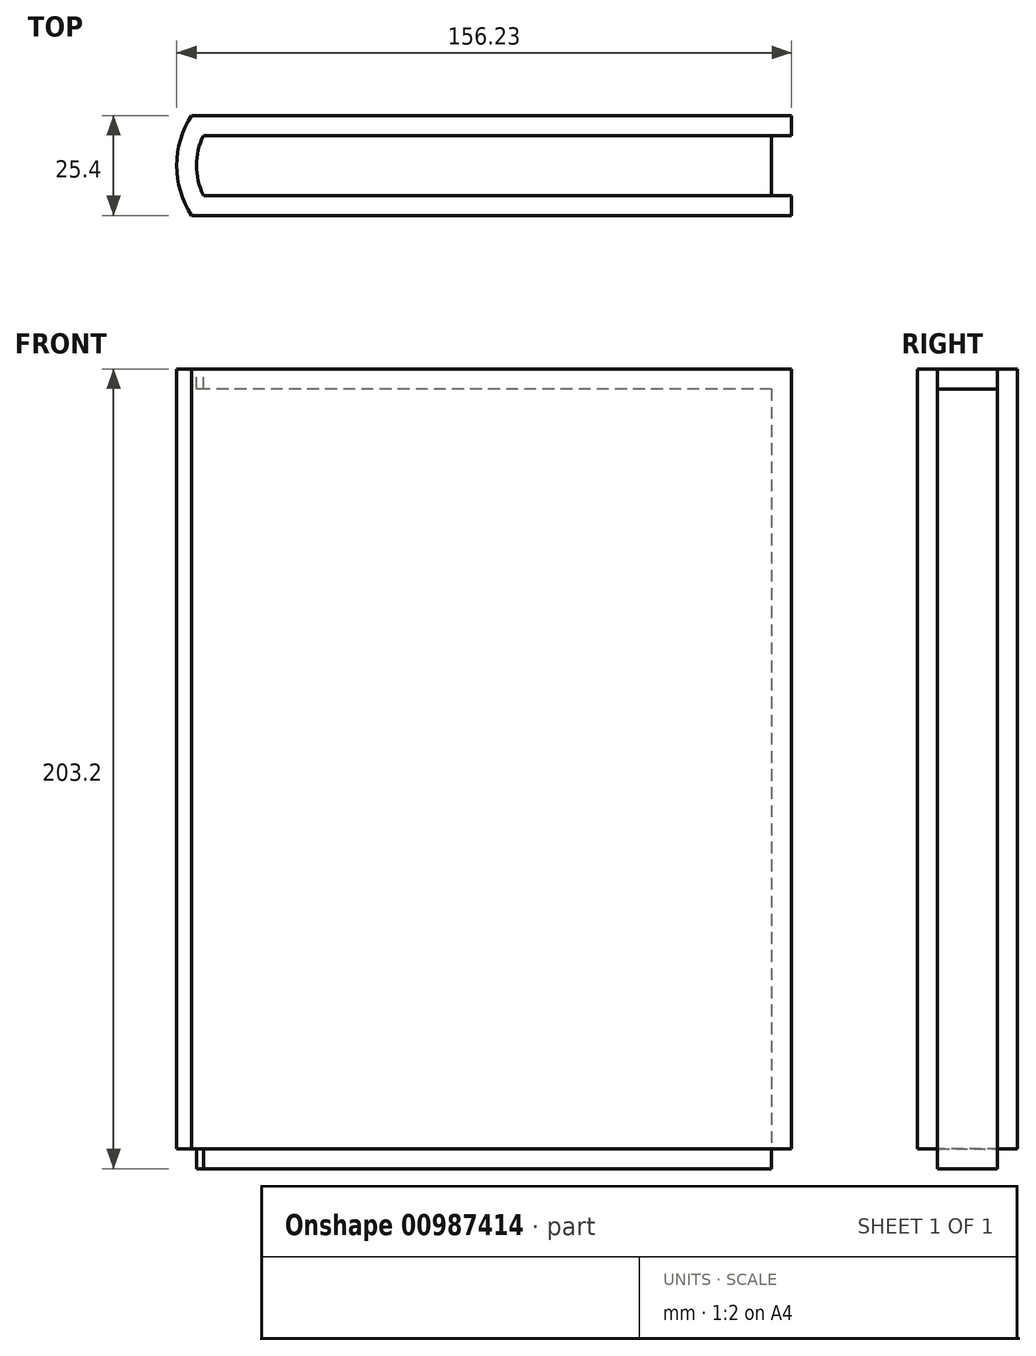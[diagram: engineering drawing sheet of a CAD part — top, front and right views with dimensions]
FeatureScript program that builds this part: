
annotation { "Feature Type Name" : "Feature", "Feature Type Description" : "" }
export const myFeature = defineFeature(function(context is Context, id is Id, definition is map)
    precondition{}
    {
        {
            var Q0;
            Q0=qCreatedBy(makeId("Front.planeOp"),FACE);
            var sketch = newSketch(context, id + "F0", { "sketchPlane" : qUnion([Q0])});
            skLineSegment(sketch, "E0.bottom", {"start": v(-106.7, 172.59) * mm, "end": v(45.7, 172.59) * mm});
            skLineSegment(sketch, "E0.top", {"start": v(-106.7, -30.61) * mm, "end": v(45.7, -30.61) * mm});
            skLineSegment(sketch, "E0.left", {"start": v(-106.7, 172.59) * mm, "end": v(-106.7, -30.61) * mm});
            skLineSegment(sketch, "E0.right", {"start": v(45.7, 172.59) * mm, "end": v(45.7, -30.61) * mm});
            skSolve(sketch);
        }
        {
            var Q0;
            Q0=makeQuery(id+"F0.imprint","IMPRINT",FACE,{"disambiguationData":[TD([[makeQuery(id+"F0.imprint","IMPRINT",EDGE,{"derivedFrom":sQuery(id+"F0.wireOp",EDGE,"E0.bottom")}),-1.0]])]});
            extrude(context, id + "F1", {"entities" : qUnion([Q0]), "endBound" : BoundingType.SYMMETRIC, "depth" : 25.4 * mm, "offsetDistance" : 25.4 * mm});
        }
        {
            var Q0;
            Q0=makeQuery(id+"F1.opExtrude","SWEPT_FACE",FACE,{"disambiguationData":[OSD([sQuery(id+"F0.wireOp",EDGE,"E0.right")])]});
            var sketch = newSketch(context, id + "F2", { "sketchPlane" : qUnion([Q0])});
            skPoint(sketch, "E1", {"position": v(-7.62, 172.59) * mm});
            skPoint(sketch, "E2", {"position": v(7.62, 172.59) * mm});
            skLineSegment(sketch, "E3", {"start": v(-7.62, 172.59) * mm, "end": v(-7.62, -30.61) * mm});
            skLineSegment(sketch, "E4", {"start": v(7.62, 172.59) * mm, "end": v(7.62, -30.61) * mm});
            skPoint(sketch, "E5", {"position": v(-7.62, -30.61) * mm});
            skPoint(sketch, "E6", {"position": v(7.62, -30.61) * mm});
            skSolve(sketch);
        }
        {
            var Q0;
            {var subQ0=sQuery(id+"F2.wireOp",EDGE,"E3");Q0=makeQuery(id+"F2.imprint","IMPRINT",FACE,{"disambiguationData":[TD([[makeQuery(id+"F2.imprint","IMPRINT",EDGE,{"derivedFrom":subQ0}),1.0]])]});}
            extrude(context, id + "F3", {"entities" : qUnion([Q0]), "operationType" : NewBodyOperationType.REMOVE, "oppositeDirection" : true, "depth" : 5.08 * mm, "offsetDistance" : 25.4 * mm});
        }
        {
            var Q0;
            Q0=makeQuery(id+"F1.opExtrude","SWEPT_FACE",FACE,{"disambiguationData":[OSD([sQuery(id+"F0.wireOp",EDGE,"E0.bottom")])]});
            var sketch = newSketch(context, id + "F4", { "sketchPlane" : qUnion([Q0])});
            skPoint(sketch, "E7", {"position": v(-106.7, 0) * mm});
            skArc(sketch, "E8", {"start": v(-106.7, 12.7) * mm, "mid": v(-110.53, 0) * mm, "end": v(-106.7, -12.7) * mm});
            skSolve(sketch);
        }
        {
            var Q0;
            Q0=makeQuery(id+"F4.imprint","IMPRINT",FACE,{"disambiguationData":[TD([[makeQuery(id+"F4.imprint","IMPRINT",EDGE,{"derivedFrom":sQuery(id+"F4.wireOp",EDGE,"E8")}),1.0]])]});
            extrude(context, id + "F5", {"entities" : qUnion([Q0]), "operationType" : NewBodyOperationType.ADD, "oppositeDirection" : true, "depth" : 203.2 * mm, "offsetDistance" : 25.4 * mm});
        }
        {
            var Q0;
            {var subQ0=sQuery(id+"F0.wireOp",EDGE,"E0.bottom");Q0=makeQuery(id+"F5.boolean.opBoolean","MERGE",FACE,{"derivedFrom":[makeQuery(id+"F1.opExtrude","SWEPT_FACE",FACE,{"disambiguationData":[OSD([subQ0])]}),makeQuery(id+"F5.opExtrude","CAP_FACE",FACE,{"disambiguationData":[OSD([subQ0,sQuery(id+"F0.wireOp",EDGE,"E0.left"),sQuery(id+"F4.wireOp",EDGE,"E8")])],"isStart":true})]});}
            var sketch = newSketch(context, id + "F6", { "sketchPlane" : qUnion([Q0])});
            skArc(sketch, "E9.0", {"start": v(-103.75, 7.62) * mm, "mid": v(-105.45, 0) * mm, "end": v(-103.75, -7.62) * mm});
            skLineSegment(sketch, "E10", {"start": v(40.62, -7.62) * mm, "end": v(-103.75, -7.62) * mm});
            skLineSegment(sketch, "E11", {"start": v(40.62, 7.62) * mm, "end": v(-103.75, 7.62) * mm});
            skSolve(sketch);
        }
        {
            var Q0;
            Q0=makeQuery(id+"F6.imprint","IMPRINT",FACE,{"disambiguationData":[TD([[makeQuery(id+"F6.imprint","IMPRINT",EDGE,{"derivedFrom":sQuery(id+"F6.wireOp",EDGE,"E9.0")}),1.0]])]});
            extrude(context, id + "F7", {"entities" : qUnion([Q0]), "operationType" : NewBodyOperationType.REMOVE, "oppositeDirection" : true, "depth" : 5.08 * mm, "offsetDistance" : 25.4 * mm});
        }
        {
            var Q0;
            Q0=makeQuery(id+"F5.boolean.opBoolean","MERGE",FACE,{"derivedFrom":[makeQuery(id+"F1.opExtrude","SWEPT_FACE",FACE,{"disambiguationData":[OSD([sQuery(id+"F0.wireOp",EDGE,"E0.top")])]}),makeQuery(id+"F5.opExtrude","CAP_FACE",FACE,{"disambiguationData":[OSD([sQuery(id+"F0.wireOp",EDGE,"E0.bottom"),sQuery(id+"F0.wireOp",EDGE,"E0.left"),sQuery(id+"F4.wireOp",EDGE,"E8")])],"isStart":false})]});
            var sketch = newSketch(context, id + "F8", { "sketchPlane" : qUnion([Q0])});
            skArc(sketch, "E12.0", {"start": v(-103.75, -7.62) * mm, "mid": v(-105.45, 0) * mm, "end": v(-103.75, 7.62) * mm});
            skLineSegment(sketch, "E13", {"start": v(40.62, -7.62) * mm, "end": v(-103.75, -7.62) * mm});
            skLineSegment(sketch, "E14", {"start": v(40.62, 7.62) * mm, "end": v(-103.75, 7.62) * mm});
            skSolve(sketch);
        }
        {
            var Q0;
            Q0=makeQuery(id+"F8.imprint","IMPRINT",FACE,{"disambiguationData":[TD([[makeQuery(id+"F8.imprint","IMPRINT",EDGE,{"derivedFrom":sQuery(id+"F8.wireOp",EDGE,"E12.0")}),-1.0]])]});
            extrude(context, id + "F9", {"entities" : qUnion([Q0]), "operationType" : NewBodyOperationType.REMOVE, "oppositeDirection" : true, "depth" : 5.08 * mm, "offsetDistance" : 25.4 * mm});
        }
    });
